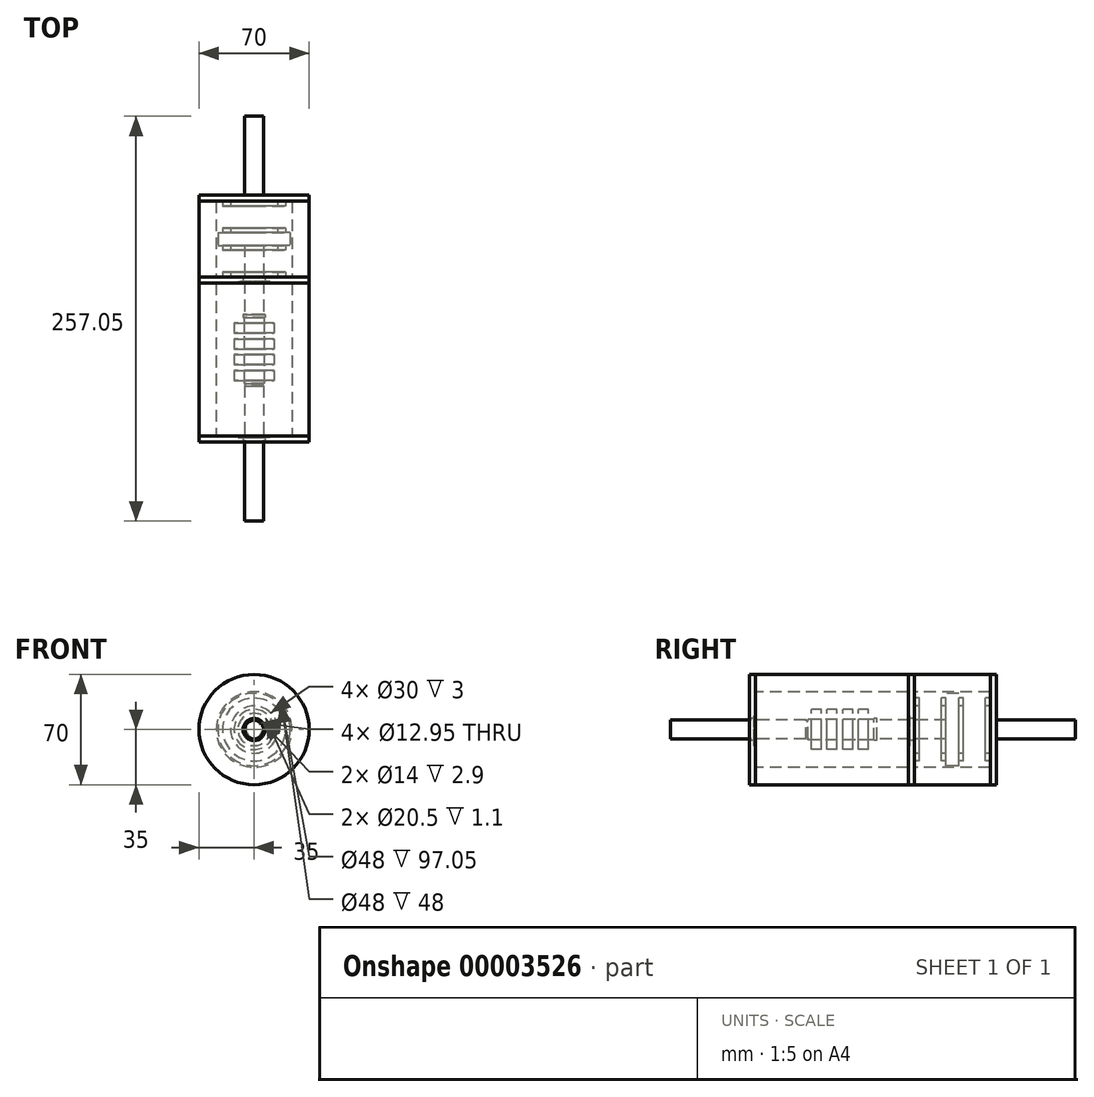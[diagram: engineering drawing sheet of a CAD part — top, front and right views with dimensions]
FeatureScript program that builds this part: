
annotation { "Feature Type Name" : "Feature", "Feature Type Description" : "" }
export const myFeature = defineFeature(function(context is Context, id is Id, definition is map)
    precondition{}
    {
        {
            var Q0;
            Q0=qCreatedBy(makeId("Right.planeOp"),FACE);
            var sketch = newSketch(context, id + "F0", { "sketchPlane" : qUnion([Q0])});
            skLineSegment(sketch, "E0", {"start": v(0, 24) * mm, "end": v(97.05, 24) * mm});
            skLineSegment(sketch, "E1", {"start": v(97.05, 24) * mm, "end": v(97.05, 35) * mm});
            skLineSegment(sketch, "E2", {"start": v(97.05, 35) * mm, "end": v(0, 35) * mm});
            skLineSegment(sketch, "E3", {"start": v(0, 35) * mm, "end": v(0, 24) * mm});
            skLineSegment(sketch, "E4.bottom", {"start": v(35.35, 12.7) * mm, "end": v(41.7, 12.7) * mm});
            skLineSegment(sketch, "E4.top", {"start": v(35.35, 6.47) * mm, "end": v(41.7, 6.47) * mm});
            skLineSegment(sketch, "E4.left", {"start": v(35.35, 12.7) * mm, "end": v(35.35, 6.47) * mm});
            skLineSegment(sketch, "E4.right", {"start": v(41.7, 12.7) * mm, "end": v(41.7, 6.47) * mm});
            skLineSegment(sketch, "E5.bottom", {"start": v(45.35, 12.7) * mm, "end": v(51.7, 12.7) * mm});
            skLineSegment(sketch, "E5.top", {"start": v(45.35, 6.47) * mm, "end": v(51.7, 6.47) * mm});
            skLineSegment(sketch, "E5.left", {"start": v(45.35, 12.7) * mm, "end": v(45.35, 6.47) * mm});
            skLineSegment(sketch, "E5.right", {"start": v(51.7, 12.7) * mm, "end": v(51.7, 6.47) * mm});
            skLineSegment(sketch, "E6.bottom", {"start": v(55.35, 12.7) * mm, "end": v(61.7, 12.7) * mm});
            skLineSegment(sketch, "E6.top", {"start": v(55.35, 6.47) * mm, "end": v(61.7, 6.47) * mm});
            skLineSegment(sketch, "E6.left", {"start": v(55.35, 12.7) * mm, "end": v(55.35, 6.47) * mm});
            skLineSegment(sketch, "E6.right", {"start": v(61.7, 12.7) * mm, "end": v(61.7, 6.47) * mm});
            skLineSegment(sketch, "E7.bottom", {"start": v(65.35, 6.48) * mm, "end": v(71.7, 6.48) * mm});
            skLineSegment(sketch, "E7.top", {"start": v(65.35, 12.7) * mm, "end": v(71.7, 12.7) * mm});
            skLineSegment(sketch, "E7.left", {"start": v(65.35, 6.47) * mm, "end": v(65.35, 12.7) * mm});
            skLineSegment(sketch, "E7.right", {"start": v(71.7, 6.48) * mm, "end": v(71.7, 12.7) * mm});
            skLineSegment(sketch, "E8", {"start": v(41.7, 6.47) * mm, "end": v(45.35, 6.47) * mm, "construction": true});
            skLineSegment(sketch, "E9", {"start": v(51.7, 6.47) * mm, "end": v(55.35, 6.47) * mm, "construction": true});
            skLineSegment(sketch, "E10", {"start": v(61.7, 6.47) * mm, "end": v(65.35, 6.47) * mm, "construction": true});
            skLineSegment(sketch, "E11.bottom", {"start": v(-54, 6) * mm, "end": v(31.85, 6) * mm});
            skLineSegment(sketch, "E11.top", {"start": v(-54, 0) * mm, "end": v(129.05, 0) * mm});
            skLineSegment(sketch, "E11.left", {"start": v(-54, 6) * mm, "end": v(-54, 0) * mm});
            skLineSegment(sketch, "E11.right", {"start": v(129.05, 23) * mm, "end": v(129.05, 20) * mm});
            skLineSegment(sketch, "E12.bottom", {"start": v(97.05, 35) * mm, "end": v(101.05, 35) * mm});
            skLineSegment(sketch, "E12.top", {"start": v(98.15, 7) * mm, "end": v(101.05, 7) * mm});
            skLineSegment(sketch, "E12.left", {"start": v(97.05, 35) * mm, "end": v(97.05, 10.25) * mm});
            skLineSegment(sketch, "E12.right", {"start": v(101.05, 35) * mm, "end": v(101.05, 20) * mm});
            skLineSegment(sketch, "E13.bottom", {"start": v(101.05, 35) * mm, "end": v(149.05, 35) * mm});
            skLineSegment(sketch, "E13.top", {"start": v(101.05, 24) * mm, "end": v(149.05, 24) * mm});
            skLineSegment(sketch, "E13.left", {"start": v(101.05, 35) * mm, "end": v(101.05, 24) * mm});
            skLineSegment(sketch, "E13.right", {"start": v(149.05, 35) * mm, "end": v(149.05, 24) * mm});
            skLineSegment(sketch, "E14.bottom", {"start": v(0, 35) * mm, "end": v(-4, 35) * mm});
            skLineSegment(sketch, "E14.top", {"start": v(-1.1, 7) * mm, "end": v(-4, 7) * mm});
            skLineSegment(sketch, "E14.left", {"start": v(0, 35) * mm, "end": v(0, 10.25) * mm});
            skLineSegment(sketch, "E14.right", {"start": v(-4, 35) * mm, "end": v(-4, 7) * mm});
            skLineSegment(sketch, "E15", {"start": v(121.05, 6) * mm, "end": v(121.05, 15) * mm});
            skLineSegment(sketch, "E16", {"start": v(121.05, 23) * mm, "end": v(129.05, 23) * mm});
            skLineSegment(sketch, "E17.bottom", {"start": v(149.05, 35) * mm, "end": v(153.05, 35) * mm});
            skLineSegment(sketch, "E17.top", {"start": v(149.05, 0) * mm, "end": v(153.05, 0) * mm});
            skLineSegment(sketch, "E17.left", {"start": v(149.05, 35) * mm, "end": v(149.05, 20) * mm});
            skLineSegment(sketch, "E17.right", {"start": v(153.05, 35) * mm, "end": v(153.05, 0) * mm});
            skLineSegment(sketch, "E18.bottom", {"start": v(101.05, 20) * mm, "end": v(104.05, 20) * mm});
            skLineSegment(sketch, "E18.top", {"start": v(101.05, 15) * mm, "end": v(104.05, 15) * mm});
            skLineSegment(sketch, "E18.right", {"start": v(104.05, 20) * mm, "end": v(104.05, 15) * mm});
            skLineSegment(sketch, "E19.bottom", {"start": v(146.05, 20) * mm, "end": v(149.05, 20) * mm});
            skLineSegment(sketch, "E19.top", {"start": v(146.05, 15) * mm, "end": v(149.05, 15) * mm});
            skLineSegment(sketch, "E19.left", {"start": v(146.05, 20) * mm, "end": v(146.05, 15) * mm});
            skLineSegment(sketch, "E20.trimOffspring", {"start": v(149.05, 15) * mm, "end": v(149.05, 0) * mm});
            skLineSegment(sketch, "E21.trimOffspring", {"start": v(101.05, 15) * mm, "end": v(101.05, 7) * mm});
            skLineSegment(sketch, "E22", {"start": v(121.05, 20) * mm, "end": v(118.05, 20) * mm});
            skLineSegment(sketch, "E23", {"start": v(118.05, 20) * mm, "end": v(118.05, 15) * mm});
            skLineSegment(sketch, "E24", {"start": v(118.05, 15) * mm, "end": v(121.05, 15) * mm});
            skLineSegment(sketch, "E25", {"start": v(129.05, 20) * mm, "end": v(132.05, 20) * mm});
            skLineSegment(sketch, "E26", {"start": v(132.05, 20) * mm, "end": v(132.05, 15) * mm});
            skLineSegment(sketch, "E27", {"start": v(132.05, 15) * mm, "end": v(129.05, 15) * mm});
            skLineSegment(sketch, "E28.trimOffspring", {"start": v(121.05, 20) * mm, "end": v(121.05, 23) * mm});
            skLineSegment(sketch, "E29.trimOffspring", {"start": v(129.05, 15) * mm, "end": v(129.05, 0) * mm});
            skLineSegment(sketch, "E30", {"start": v(101.05, 7) * mm, "end": v(121.05, 7) * mm, "construction": true});
            skLineSegment(sketch, "E31", {"start": v(129.05, 7) * mm, "end": v(149.05, 7) * mm, "construction": true});
            skLineSegment(sketch, "E32.bottom", {"start": v(153.05, 0) * mm, "end": v(203.05, 0) * mm});
            skLineSegment(sketch, "E32.top", {"start": v(153.05, 6) * mm, "end": v(203.05, 6) * mm});
            skLineSegment(sketch, "E32.left", {"start": v(153.05, 0) * mm, "end": v(153.05, 6) * mm});
            skLineSegment(sketch, "E32.right", {"start": v(203.05, 0) * mm, "end": v(203.05, 6) * mm});
            skLineSegment(sketch, "E33", {"start": v(-1.1, 7) * mm, "end": v(-1.1, 10.25) * mm});
            skLineSegment(sketch, "E34", {"start": v(-1.1, 10.25) * mm, "end": v(0, 10.25) * mm});
            skLineSegment(sketch, "E35", {"start": v(97.05, 10.25) * mm, "end": v(98.15, 10.25) * mm});
            skLineSegment(sketch, "E36", {"start": v(98.15, 10.25) * mm, "end": v(98.15, 7) * mm});
            skLineSegment(sketch, "E37", {"start": v(77.05, 7) * mm, "end": v(77.05, 6) * mm});
            skLineSegment(sketch, "E38", {"start": v(33.3, 6.47) * mm, "end": v(75.05, 6.47) * mm});
            skLineSegment(sketch, "E39", {"start": v(33.3, 6.47) * mm, "end": v(33.3, 5.75) * mm});
            skLineSegment(sketch, "E40.trimOffspring", {"start": v(77.05, 6) * mm, "end": v(121.05, 6) * mm});
            skLineSegment(sketch, "E41", {"start": v(75.05, 6.47) * mm, "end": v(75.05, 7) * mm});
            skLineSegment(sketch, "E42", {"start": v(75.05, 7) * mm, "end": v(77.05, 7) * mm});
            skLineSegment(sketch, "E43", {"start": v(31.85, 6) * mm, "end": v(32.45, 5.4) * mm});
            skArc(sketch, "E44", {"start": v(32.45, 5.4) * mm, "mid": v(33, 5.29) * mm, "end": v(33.3, 5.75) * mm});
            skPoint(sketch, "E45.orphan", {"position": v(33.3, 6) * mm});
            skLineSegment(sketch, "E46", {"start": v(77.05, 7) * mm, "end": v(97.05, 7) * mm, "construction": true});
            skLineSegment(sketch, "E47", {"start": v(35.35, 12.7) * mm, "end": v(32, 12.7) * mm, "construction": true});
            skLineSegment(sketch, "E48", {"start": v(32, 12.7) * mm, "end": v(20, 12.7) * mm, "construction": true});
            skLineSegment(sketch, "E49", {"start": v(20, 12.7) * mm, "end": v(0, 12.7) * mm, "construction": true});
            skLineSegment(sketch, "E50.bottom", {"start": v(39.52, 23.2) * mm, "end": v(47.52, 23.2) * mm});
            skLineSegment(sketch, "E50.top", {"start": v(39.52, 13.2) * mm, "end": v(47.52, 13.2) * mm});
            skLineSegment(sketch, "E50.left", {"start": v(39.52, 23.2) * mm, "end": v(39.52, 13.2) * mm});
            skLineSegment(sketch, "E50.right", {"start": v(47.52, 23.2) * mm, "end": v(47.52, 13.2) * mm});
            skLineSegment(sketch, "E51", {"start": v(43.52, 23.2) * mm, "end": v(43.52, 13.2) * mm, "construction": true});
            skLineSegment(sketch, "E52", {"start": v(38.53, 12.7) * mm, "end": v(38.53, 6.47) * mm, "construction": true});
            skLineSegment(sketch, "E53.bottom", {"start": v(49.52, 13.2) * mm, "end": v(57.52, 13.2) * mm});
            skLineSegment(sketch, "E53.top", {"start": v(49.52, 23.2) * mm, "end": v(57.52, 23.2) * mm});
            skLineSegment(sketch, "E53.left", {"start": v(49.52, 13.2) * mm, "end": v(49.52, 23.2) * mm});
            skLineSegment(sketch, "E53.right", {"start": v(57.52, 13.2) * mm, "end": v(57.52, 23.2) * mm});
            skLineSegment(sketch, "E54.bottom", {"start": v(59.53, 13.2) * mm, "end": v(67.53, 13.2) * mm});
            skLineSegment(sketch, "E54.top", {"start": v(59.52, 23.2) * mm, "end": v(67.52, 23.2) * mm});
            skLineSegment(sketch, "E54.left", {"start": v(59.52, 13.2) * mm, "end": v(59.52, 23.2) * mm});
            skLineSegment(sketch, "E54.right", {"start": v(67.53, 13.2) * mm, "end": v(67.53, 23.2) * mm});
            skLineSegment(sketch, "E55", {"start": v(48.52, 12.7) * mm, "end": v(48.52, 6.47) * mm, "construction": true});
            skLineSegment(sketch, "E56", {"start": v(53.52, 23.2) * mm, "end": v(53.52, 13.2) * mm, "construction": true});
            skLineSegment(sketch, "E57", {"start": v(47.52, 13.2) * mm, "end": v(49.52, 13.2) * mm, "construction": true});
            skLineSegment(sketch, "E58", {"start": v(57.52, 13.2) * mm, "end": v(59.53, 13.2) * mm, "construction": true});
            skLineSegment(sketch, "E59", {"start": v(61.7, 12.7) * mm, "end": v(65.35, 12.7) * mm, "construction": true});
            skLineSegment(sketch, "E60", {"start": v(53.53, 6.47) * mm, "end": v(53.53, 12.7) * mm, "construction": true});
            skSolve(sketch);
        }
        {
            var Q0;
            Q0=makeQuery(id+"F0.imprint","IMPRINT",FACE,{"disambiguationData":[TD([[makeQuery(id+"F0.imprint","IMPRINT",EDGE,{"derivedFrom":sQuery(id+"F0.wireOp",EDGE,"E11.bottom")}),-1.0]])]});
            var Q1;
            Q1=sQuery(id+"F0.wireOp",EDGE,"E11.top");
            revolve(context, id + "F1", {"entities" : qUnion([Q0]), "axis" : qUnion([Q1]), "revolveType" : RevolveType.FULL});
        }
        {
            var Q0;
            {var subQ2=sQuery(id+"F0.wireOp",EDGE,"E14.bottom");Q0=makeQuery(id+"F0.imprint","IMPRINT",FACE,{"disambiguationData":[TD([[makeQuery(id+"F0.imprint","IMPRINT",EDGE,{"derivedFrom":subQ2}),1.0]])]});}
            var Q1;
            Q1=sQuery(id+"F0.wireOp",EDGE,"E32.bottom");
            revolve(context, id + "F2", {"entities" : qUnion([Q0]), "axis" : qUnion([Q1]), "revolveType" : RevolveType.FULL});
        }
        {
            var Q0;
            {var subQ2=sQuery(id+"F0.wireOp",EDGE,"E12.bottom");Q0=makeQuery(id+"F0.imprint","IMPRINT",FACE,{"disambiguationData":[TD([[makeQuery(id+"F0.imprint","IMPRINT",EDGE,{"derivedFrom":subQ2}),-1.0]])]});}
            var Q1;
            Q1=sQuery(id+"F0.wireOp",EDGE,"E32.bottom");
            revolve(context, id + "F3", {"entities" : qUnion([Q0]), "axis" : qUnion([Q1]), "revolveType" : RevolveType.FULL});
        }
        {
            var Q0;
            {var subQ2=sQuery(id+"F0.wireOp",EDGE,"E0");Q0=makeQuery(id+"F0.imprint","IMPRINT",FACE,{"disambiguationData":[TD([[makeQuery(id+"F0.imprint","IMPRINT",EDGE,{"derivedFrom":subQ2}),1.0]])]});}
            var Q1;
            Q1=sQuery(id+"F0.wireOp",EDGE,"E32.bottom");
            revolve(context, id + "F4", {"entities" : qUnion([Q0]), "axis" : qUnion([Q1]), "revolveType" : RevolveType.FULL});
        }
        {
            var Q0;
            {var subQ2=sQuery(id+"F0.wireOp",EDGE,"E13.bottom");Q0=makeQuery(id+"F0.imprint","IMPRINT",FACE,{"disambiguationData":[TD([[makeQuery(id+"F0.imprint","IMPRINT",EDGE,{"derivedFrom":subQ2}),-1.0]])]});}
            var Q1;
            Q1=sQuery(id+"F0.wireOp",EDGE,"E32.bottom");
            revolve(context, id + "F5", {"entities" : qUnion([Q0]), "axis" : qUnion([Q1]), "revolveType" : RevolveType.FULL});
        }
        {
            var Q0;
            {var subQ3=sQuery(id+"F0.wireOp",EDGE,"E17.bottom");Q0=makeQuery(id+"F0.imprint","IMPRINT",FACE,{"disambiguationData":[TD([[makeQuery(id+"F0.imprint","IMPRINT",EDGE,{"derivedFrom":subQ3}),-1.0]])]});}
            var Q1;
            Q1=sQuery(id+"F0.wireOp",EDGE,"E32.bottom");
            revolve(context, id + "F6", {"entities" : qUnion([Q0]), "axis" : qUnion([Q1]), "revolveType" : RevolveType.FULL});
        }
        {
            var Q0;
            Q0=makeQuery(id+"F0.imprint","IMPRINT",FACE,{"disambiguationData":[TD([[makeQuery(id+"F0.imprint","IMPRINT",EDGE,{"derivedFrom":sQuery(id+"F0.wireOp",EDGE,"E32.bottom")}),1.0]])]});
            var Q1;
            Q1=sQuery(id+"F0.wireOp",EDGE,"E32.bottom");
            revolve(context, id + "F7", {"entities" : qUnion([Q0]), "axis" : qUnion([Q1]), "revolveType" : RevolveType.FULL});
        }
        {
            var Q0;
            Q0=makeQuery(id+"F0.imprint","IMPRINT",FACE,{"disambiguationData":[TD([[makeQuery(id+"F0.imprint","IMPRINT",EDGE,{"derivedFrom":sQuery(id+"F0.wireOp",EDGE,"E4.bottom")}),-1.0]])]});
            var Q1;
            Q1=makeQuery(id+"F0.imprint","IMPRINT",FACE,{"disambiguationData":[TD([[makeQuery(id+"F0.imprint","IMPRINT",EDGE,{"derivedFrom":sQuery(id+"F0.wireOp",EDGE,"E5.bottom")}),-1.0]])]});
            var Q2;
            Q2=makeQuery(id+"F0.imprint","IMPRINT",FACE,{"disambiguationData":[TD([[makeQuery(id+"F0.imprint","IMPRINT",EDGE,{"derivedFrom":sQuery(id+"F0.wireOp",EDGE,"E6.bottom")}),-1.0]])]});
            var Q3;
            Q3=makeQuery(id+"F0.imprint","IMPRINT",FACE,{"disambiguationData":[TD([[makeQuery(id+"F0.imprint","IMPRINT",EDGE,{"derivedFrom":sQuery(id+"F0.wireOp",EDGE,"E7.bottom")}),1.0]])]});
            var Q4;
            Q4=sQuery(id+"F0.wireOp",EDGE,"E32.bottom");
            revolve(context, id + "F8", {"entities" : qUnion([Q0, Q1, Q2, Q3]), "axis" : qUnion([Q4]), "revolveType" : RevolveType.FULL});
        }
    });
